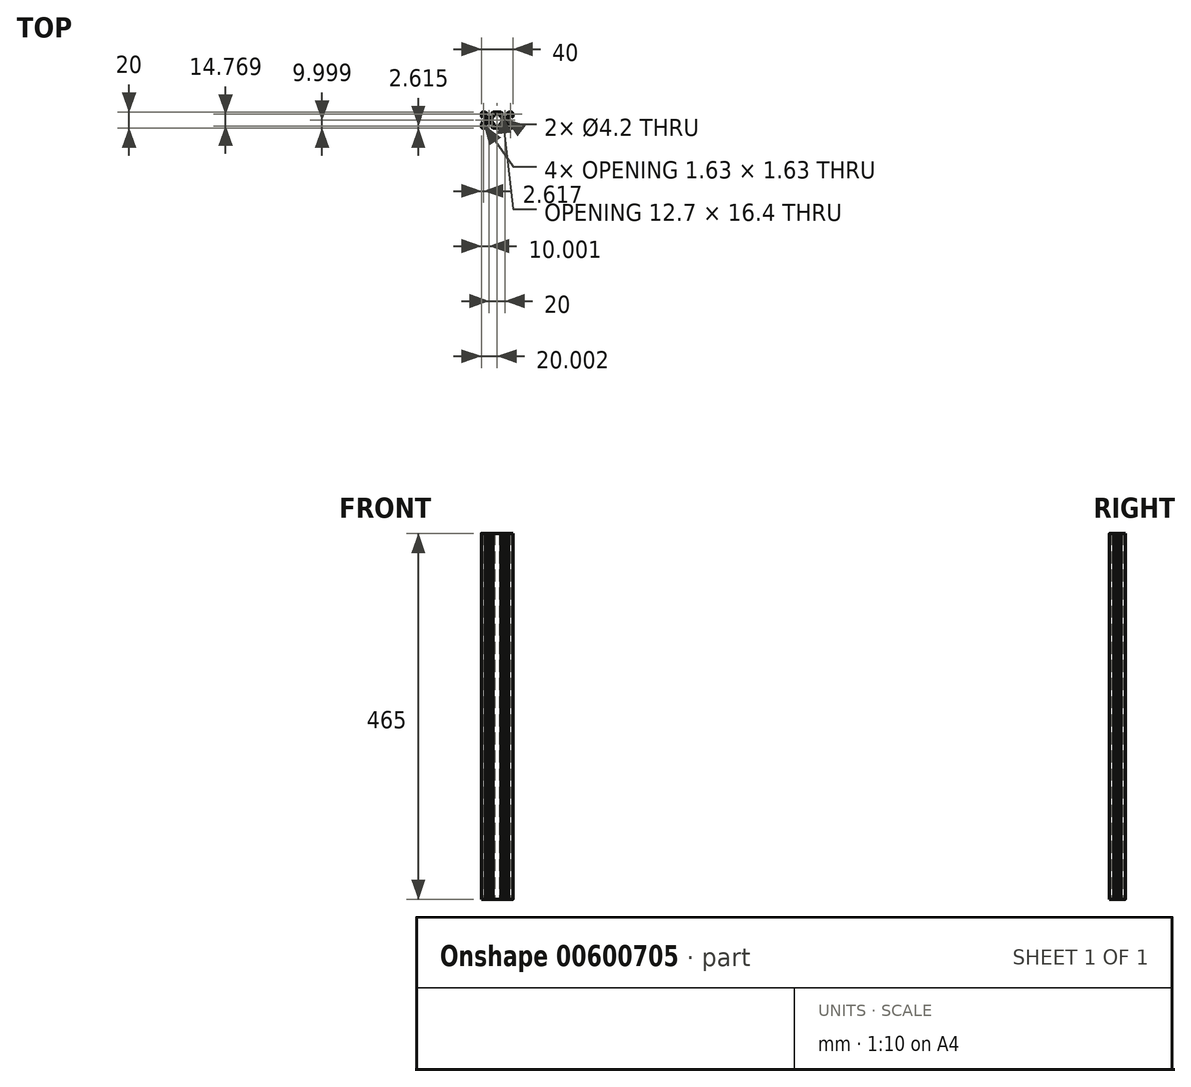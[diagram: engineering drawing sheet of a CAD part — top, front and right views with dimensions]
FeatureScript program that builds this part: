
annotation { "Feature Type Name" : "Feature", "Feature Type Description" : "" }
export const myFeature = defineFeature(function(context is Context, id is Id, definition is map)
    precondition{}
    {
        {
            var Q0;
            Q0=qCreatedBy(makeId("Top.planeOp"),FACE);
            var sketch = newSketch(context, id + "F0", { "sketchPlane" : qUnion([Q0])});
            skLineSegment(sketch, "E0", {"start": v(-1.54, -10.06) * mm, "end": v(-5.4, -10.06) * mm});
            skLineSegment(sketch, "E1", {"start": v(-20.04, -8.56) * mm, "end": v(-20.04, -4.7) * mm});
            skLineSegment(sketch, "E2", {"start": v(-18.54, 9.94) * mm, "end": v(-14.68, 9.94) * mm});
            skLineSegment(sketch, "E3.0", {"start": v(-15.54, 8.14) * mm, "end": v(-12.88, 8.14) * mm});
            skLineSegment(sketch, "E3.1", {"start": v(-18.24, -5.56) * mm, "end": v(-18.24, -2.9) * mm});
            skLineSegment(sketch, "E3.2", {"start": v(-4.54, -8.26) * mm, "end": v(-7.2, -8.26) * mm});
            skLineSegment(sketch, "E4.trimOffspring", {"start": v(-5.4, 9.94) * mm, "end": v(-1.54, 9.94) * mm});
            skLineSegment(sketch, "E5", {"start": v(-12.88, 8.14) * mm, "end": v(-14.68, 9.94) * mm});
            skLineSegment(sketch, "E6.trimOffspring", {"start": v(-7.2, 8.14) * mm, "end": v(-4.54, 8.14) * mm});
            skLineSegment(sketch, "E7.MirrorCS", {"start": v(-7.2, 8.14) * mm, "end": v(-5.4, 9.94) * mm});
            skLineSegment(sketch, "E8.MirrorCS", {"start": v(-7.2, -8.26) * mm, "end": v(-5.4, -10.06) * mm});
            skLineSegment(sketch, "E9.MirrorCS", {"start": v(-12.88, -8.26) * mm, "end": v(-14.68, -10.06) * mm});
            skLineSegment(sketch, "E10.trimOffspring", {"start": v(-12.88, -8.26) * mm, "end": v(-15.54, -8.26) * mm});
            skLineSegment(sketch, "E11.trimOffspring", {"start": v(-14.68, -10.06) * mm, "end": v(-18.54, -10.06) * mm});
            skLineSegment(sketch, "E12", {"start": v(-18.24, 2.78) * mm, "end": v(-20.04, 4.58) * mm});
            skLineSegment(sketch, "E13", {"start": v(-18.24, -2.9) * mm, "end": v(-20.04, -4.7) * mm});
            skLineSegment(sketch, "E14.trimOffspring", {"start": v(-20.04, 4.58) * mm, "end": v(-20.04, 8.44) * mm});
            skLineSegment(sketch, "E15.trimOffspring", {"start": v(-18.24, 2.78) * mm, "end": v(-18.24, 5.44) * mm});
            skCircle(sketch, "E16", {"center": v(-10.04, -0.06) * mm, "radius": 2.1 * mm});
            skLineSegment(sketch, "E17", {"start": v(-16.6, 5.44) * mm, "end": v(-13.94, 2.78) * mm});
            skLineSegment(sketch, "E18", {"start": v(-15.54, 6.5) * mm, "end": v(-12.88, 3.84) * mm});
            skLineSegment(sketch, "E19", {"start": v(-15.54, 6.5) * mm, "end": v(-15.54, 8.14) * mm});
            skLineSegment(sketch, "E20", {"start": v(-16.6, 5.44) * mm, "end": v(-18.24, 5.44) * mm});
            skLineSegment(sketch, "E21", {"start": v(-3.48, 5.44) * mm, "end": v(-6.14, 2.78) * mm});
            skLineSegment(sketch, "E22", {"start": v(-4.54, 6.5) * mm, "end": v(-7.2, 3.84) * mm});
            skLineSegment(sketch, "E23", {"start": v(-16.6, -5.56) * mm, "end": v(-18.24, -5.56) * mm});
            skLineSegment(sketch, "E24", {"start": v(-15.54, -6.62) * mm, "end": v(-15.54, -8.26) * mm});
            skLineSegment(sketch, "E25", {"start": v(-4.54, 6.5) * mm, "end": v(-4.54, 8.14) * mm});
            skLineSegment(sketch, "E26", {"start": v(-4.54, -6.62) * mm, "end": v(-4.54, -8.26) * mm});
            skLineSegment(sketch, "E27.trimOffspring", {"start": v(-7.2, -3.96) * mm, "end": v(-4.54, -6.62) * mm});
            skLineSegment(sketch, "E28.trimOffspring", {"start": v(-12.88, -3.96) * mm, "end": v(-15.54, -6.62) * mm});
            skLineSegment(sketch, "E29.trimOffspring", {"start": v(-13.94, -2.9) * mm, "end": v(-16.6, -5.56) * mm});
            skLineSegment(sketch, "E30.trimOffspring", {"start": v(-6.14, -2.9) * mm, "end": v(-3.48, -5.56) * mm});
            skLineSegment(sketch, "E31", {"start": v(-13.94, -2.9) * mm, "end": v(-13.94, -0.31) * mm});
            skLineSegment(sketch, "E32", {"start": v(-12.88, 3.84) * mm, "end": v(-10.29, 3.84) * mm});
            skLineSegment(sketch, "E33", {"start": v(-12.88, -3.96) * mm, "end": v(-10.29, -3.96) * mm});
            skLineSegment(sketch, "E34", {"start": v(-6.14, 2.78) * mm, "end": v(-6.14, 0.19) * mm});
            skLineSegment(sketch, "E35", {"start": v(-18.24, 6.5) * mm, "end": v(-18.24, 8.14) * mm});
            skLineSegment(sketch, "E36", {"start": v(-16.6, 8.14) * mm, "end": v(-18.24, 8.14) * mm});
            skLineSegment(sketch, "E37", {"start": v(-18.24, 6.5) * mm, "end": v(-17.67, 6.5) * mm});
            skLineSegment(sketch, "E38", {"start": v(-16.6, 8.14) * mm, "end": v(-16.6, 7.57) * mm});
            skLineSegment(sketch, "E39", {"start": v(-17.67, 6.5) * mm, "end": v(-16.6, 7.57) * mm});
            skLineSegment(sketch, "E40.MirrorCS", {"start": v(-16.6, -8.26) * mm, "end": v(-18.24, -8.26) * mm});
            skLineSegment(sketch, "E41.MirrorCS", {"start": v(-18.24, -6.63) * mm, "end": v(-17.67, -6.63) * mm});
            skLineSegment(sketch, "E42.MirrorCS", {"start": v(-18.24, -6.63) * mm, "end": v(-18.24, -8.26) * mm});
            skLineSegment(sketch, "E43.MirrorCS", {"start": v(-17.67, -6.63) * mm, "end": v(-16.6, -7.7) * mm});
            skLineSegment(sketch, "E44.MirrorCS", {"start": v(-16.6, -8.26) * mm, "end": v(-16.6, -7.7) * mm});
            skArc(sketch, "E45.filletArc", {"start": v(-18.54, 9.94) * mm, "mid": v(-19.6, 9.5) * mm, "end": v(-20.04, 8.44) * mm});
            skPoint(sketch, "E46.visualSharp", {"position": v(-0.04, 9.94) * mm});
            skArc(sketch, "E47.filletArc", {"start": v(-20.04, -8.56) * mm, "mid": v(-19.6, -9.62) * mm, "end": v(-18.54, -10.06) * mm});
            skLineSegment(sketch, "E48", {"start": v(-13.69, -0.06) * mm, "end": v(-13.94, 0.19) * mm});
            skLineSegment(sketch, "E49.MirrorCS", {"start": v(-13.69, -0.06) * mm, "end": v(-13.94, -0.31) * mm});
            skLineSegment(sketch, "E50.trimOffspring", {"start": v(-13.94, 0.19) * mm, "end": v(-13.94, 2.78) * mm});
            skLineSegment(sketch, "E51.MirrorCS", {"start": v(-6.39, -0.06) * mm, "end": v(-6.14, 0.19) * mm});
            skLineSegment(sketch, "E52.MirrorCS", {"start": v(-6.39, -0.06) * mm, "end": v(-6.14, -0.31) * mm});
            skLineSegment(sketch, "E53", {"start": v(-10.04, -3.71) * mm, "end": v(-9.79, -3.96) * mm});
            skLineSegment(sketch, "E54.MirrorCS", {"start": v(-10.04, -3.71) * mm, "end": v(-10.29, -3.96) * mm});
            skLineSegment(sketch, "E55.trimOffspring", {"start": v(-9.79, -3.96) * mm, "end": v(-7.2, -3.96) * mm});
            skLineSegment(sketch, "E56.trimOffspring", {"start": v(-6.14, -0.31) * mm, "end": v(-6.14, -2.9) * mm});
            skLineSegment(sketch, "E57.MirrorCS", {"start": v(-10.04, 3.59) * mm, "end": v(-10.29, 3.84) * mm});
            skLineSegment(sketch, "E58.MirrorCS", {"start": v(-10.04, 3.59) * mm, "end": v(-9.79, 3.84) * mm});
            skLineSegment(sketch, "E59.trimOffspring", {"start": v(-9.79, 3.84) * mm, "end": v(-7.2, 3.84) * mm});
            skLineSegment(sketch, "E60.MirrorCS", {"start": v(9.96, -3.71) * mm, "end": v(9.71, -3.96) * mm});
            skLineSegment(sketch, "E61.MirrorCS", {"start": v(9.96, -3.71) * mm, "end": v(10.21, -3.96) * mm});
            skLineSegment(sketch, "E62.MirrorCS", {"start": v(13.61, -0.06) * mm, "end": v(13.86, 0.19) * mm});
            skLineSegment(sketch, "E63.MirrorCS", {"start": v(13.61, -0.06) * mm, "end": v(13.86, -0.31) * mm});
            skLineSegment(sketch, "E64.MirrorCS", {"start": v(6.31, -0.06) * mm, "end": v(6.06, 0.19) * mm});
            skLineSegment(sketch, "E65.MirrorCS", {"start": v(6.31, -0.06) * mm, "end": v(6.06, -0.31) * mm});
            skLineSegment(sketch, "E66.MirrorCS", {"start": v(18.16, -6.63) * mm, "end": v(17.6, -6.63) * mm});
            skLineSegment(sketch, "E67.MirrorCS", {"start": v(9.96, 3.59) * mm, "end": v(10.21, 3.84) * mm});
            skLineSegment(sketch, "E68.MirrorCS", {"start": v(9.96, 3.59) * mm, "end": v(9.71, 3.84) * mm});
            skLineSegment(sketch, "E69.MirrorCS", {"start": v(18.16, 6.5) * mm, "end": v(17.6, 6.5) * mm});
            skLineSegment(sketch, "E70.MirrorCS", {"start": v(16.53, -8.26) * mm, "end": v(16.53, -7.7) * mm});
            skLineSegment(sketch, "E71.MirrorCS", {"start": v(16.53, 8.14) * mm, "end": v(16.53, 7.57) * mm});
            skLineSegment(sketch, "E72.MirrorCS", {"start": v(18.16, 2.78) * mm, "end": v(18.16, 5.44) * mm});
            skLineSegment(sketch, "E73.MirrorCS", {"start": v(4.46, -6.62) * mm, "end": v(4.46, -8.26) * mm});
            skArc(sketch, "E74.MirrorCS", {"start": v(19.96, -8.56) * mm, "mid": v(19.52, -9.62) * mm, "end": v(18.46, -10.06) * mm});
            skLineSegment(sketch, "E75.MirrorCS", {"start": v(7.12, -3.96) * mm, "end": v(4.46, -6.62) * mm});
            skLineSegment(sketch, "E76.MirrorCS", {"start": v(12.8, -3.96) * mm, "end": v(15.46, -6.62) * mm});
            skPoint(sketch, "E77.MirrorP", {"position": v(-0.04, -10.06) * mm});
            skLineSegment(sketch, "E78.MirrorCS", {"start": v(13.86, -2.9) * mm, "end": v(16.52, -5.56) * mm});
            skLineSegment(sketch, "E79.MirrorCS", {"start": v(13.86, 0.19) * mm, "end": v(13.86, 2.78) * mm});
            skLineSegment(sketch, "E80.MirrorCS", {"start": v(6.06, -2.9) * mm, "end": v(3.4, -5.56) * mm});
            skCircle(sketch, "E81.MirrorC", {"center": v(9.96, -0.06) * mm, "radius": 2.1 * mm});
            skLineSegment(sketch, "E82.MirrorCS", {"start": v(13.86, -2.9) * mm, "end": v(13.86, -0.31) * mm});
            skLineSegment(sketch, "E83.MirrorCS", {"start": v(16.52, 5.44) * mm, "end": v(13.86, 2.78) * mm});
            skLineSegment(sketch, "E84.MirrorCS", {"start": v(12.8, 3.84) * mm, "end": v(10.21, 3.84) * mm});
            skLineSegment(sketch, "E85.MirrorCS", {"start": v(15.46, 6.5) * mm, "end": v(12.8, 3.84) * mm});
            skLineSegment(sketch, "E86.MirrorCS", {"start": v(12.8, -3.96) * mm, "end": v(10.21, -3.96) * mm});
            skLineSegment(sketch, "E87.MirrorCS", {"start": v(15.46, 6.5) * mm, "end": v(15.46, 8.14) * mm});
            skLineSegment(sketch, "E88.MirrorCS", {"start": v(6.06, -0.31) * mm, "end": v(6.06, -2.9) * mm});
            skLineSegment(sketch, "E89.MirrorCS", {"start": v(18.16, 6.5) * mm, "end": v(18.16, 8.14) * mm});
            skLineSegment(sketch, "E90.MirrorCS", {"start": v(3.4, 5.44) * mm, "end": v(6.06, 2.78) * mm});
            skLineSegment(sketch, "E91.MirrorCS", {"start": v(16.53, -8.26) * mm, "end": v(18.16, -8.26) * mm});
            skLineSegment(sketch, "E92.MirrorCS", {"start": v(6.06, 2.78) * mm, "end": v(6.06, 0.19) * mm});
            skLineSegment(sketch, "E93.MirrorCS", {"start": v(16.52, 5.44) * mm, "end": v(18.16, 5.44) * mm});
            skLineSegment(sketch, "E94.MirrorCS", {"start": v(9.71, -3.96) * mm, "end": v(7.12, -3.96) * mm});
            skLineSegment(sketch, "E95.MirrorCS", {"start": v(18.16, -6.63) * mm, "end": v(18.16, -8.26) * mm});
            skLineSegment(sketch, "E96.MirrorCS", {"start": v(16.53, 8.14) * mm, "end": v(18.16, 8.14) * mm});
            skLineSegment(sketch, "E97.MirrorCS", {"start": v(4.46, 6.5) * mm, "end": v(7.12, 3.84) * mm});
            skLineSegment(sketch, "E98.MirrorCS", {"start": v(17.6, -6.63) * mm, "end": v(16.53, -7.7) * mm});
            skLineSegment(sketch, "E99.MirrorCS", {"start": v(16.52, -5.56) * mm, "end": v(18.16, -5.56) * mm});
            skLineSegment(sketch, "E100.MirrorCS", {"start": v(12.8, -8.26) * mm, "end": v(14.6, -10.06) * mm});
            skLineSegment(sketch, "E101.MirrorCS", {"start": v(12.8, -8.26) * mm, "end": v(15.46, -8.26) * mm});
            skLineSegment(sketch, "E102.MirrorCS", {"start": v(14.6, -10.06) * mm, "end": v(18.46, -10.06) * mm});
            skLineSegment(sketch, "E103.MirrorCS", {"start": v(1.46, -10.06) * mm, "end": v(5.32, -10.06) * mm});
            skLineSegment(sketch, "E104.MirrorCS", {"start": v(19.96, -8.56) * mm, "end": v(19.96, -4.7) * mm});
            skLineSegment(sketch, "E105.MirrorCS", {"start": v(18.46, 9.94) * mm, "end": v(14.6, 9.94) * mm});
            skLineSegment(sketch, "E106.MirrorCS", {"start": v(15.46, 8.14) * mm, "end": v(12.8, 8.14) * mm});
            skLineSegment(sketch, "E107.MirrorCS", {"start": v(18.16, -5.56) * mm, "end": v(18.16, -2.9) * mm});
            skLineSegment(sketch, "E108.MirrorCS", {"start": v(4.46, -8.26) * mm, "end": v(7.12, -8.26) * mm});
            skLineSegment(sketch, "E109.MirrorCS", {"start": v(5.32, 9.94) * mm, "end": v(1.46, 9.94) * mm});
            skLineSegment(sketch, "E110.MirrorCS", {"start": v(12.8, 8.14) * mm, "end": v(14.6, 9.94) * mm});
            skLineSegment(sketch, "E111.MirrorCS", {"start": v(7.12, 8.14) * mm, "end": v(4.46, 8.14) * mm});
            skLineSegment(sketch, "E112.MirrorCS", {"start": v(7.12, 8.14) * mm, "end": v(5.32, 9.94) * mm});
            skLineSegment(sketch, "E113.MirrorCS", {"start": v(7.12, -8.26) * mm, "end": v(5.32, -10.06) * mm});
            skLineSegment(sketch, "E114.MirrorCS", {"start": v(18.16, 2.78) * mm, "end": v(19.96, 4.58) * mm});
            skLineSegment(sketch, "E115.MirrorCS", {"start": v(9.71, 3.84) * mm, "end": v(7.12, 3.84) * mm});
            skLineSegment(sketch, "E116.MirrorCS", {"start": v(15.46, -6.62) * mm, "end": v(15.46, -8.26) * mm});
            skLineSegment(sketch, "E117.MirrorCS", {"start": v(18.16, -2.9) * mm, "end": v(19.96, -4.7) * mm});
            skArc(sketch, "E118.MirrorCS", {"start": v(18.46, 9.94) * mm, "mid": v(19.52, 9.5) * mm, "end": v(19.96, 8.44) * mm});
            skLineSegment(sketch, "E119.MirrorCS", {"start": v(17.6, 6.5) * mm, "end": v(16.53, 7.57) * mm});
            skLineSegment(sketch, "E120.MirrorCS", {"start": v(4.46, 6.5) * mm, "end": v(4.46, 8.14) * mm});
            skLineSegment(sketch, "E121.MirrorCS", {"start": v(19.96, 4.58) * mm, "end": v(19.96, 8.44) * mm});
            skLineSegment(sketch, "E122", {"start": v(-1.54, 9.94) * mm, "end": v(1.46, 9.94) * mm});
            skLineSegment(sketch, "E123", {"start": v(-1.54, -10.06) * mm, "end": v(1.46, -10.06) * mm});
            skLineSegment(sketch, "E124", {"start": v(-3.04, 8.14) * mm, "end": v(2.96, 8.14) * mm});
            skLineSegment(sketch, "E125", {"start": v(-3.04, -8.26) * mm, "end": v(-3.04, -6) * mm});
            skLineSegment(sketch, "E126", {"start": v(-6.14, -2.9) * mm, "end": v(-3.04, -6) * mm});
            skLineSegment(sketch, "E127", {"start": v(2.96, -8.26) * mm, "end": v(2.96, -6) * mm});
            skLineSegment(sketch, "E128", {"start": v(6.06, -2.9) * mm, "end": v(2.96, -6) * mm});
            skLineSegment(sketch, "E129", {"start": v(-3.04, -8.26) * mm, "end": v(2.96, -8.26) * mm});
            skLineSegment(sketch, "E130", {"start": v(6.06, 2.78) * mm, "end": v(2.96, 5.88) * mm});
            skLineSegment(sketch, "E131", {"start": v(-6.14, 2.78) * mm, "end": v(-3.48, 5.44) * mm});
            skLineSegment(sketch, "E132", {"start": v(-3.48, 5.44) * mm, "end": v(-3.04, 5.88) * mm});
            skLineSegment(sketch, "E133.trimOffspring", {"start": v(-3.04, 5.88) * mm, "end": v(-3.04, 8.14) * mm});
            skLineSegment(sketch, "E134", {"start": v(2.96, 5.88) * mm, "end": v(2.96, 8.14) * mm});
            skSolve(sketch);
        }
        {
            var Q0;
            Q0=qSketchRegion(id+"F0",true);
            extrude(context, id + "F1", {"entities" : qUnion([Q0]), "depth" : 465 * mm});
        }
    });
